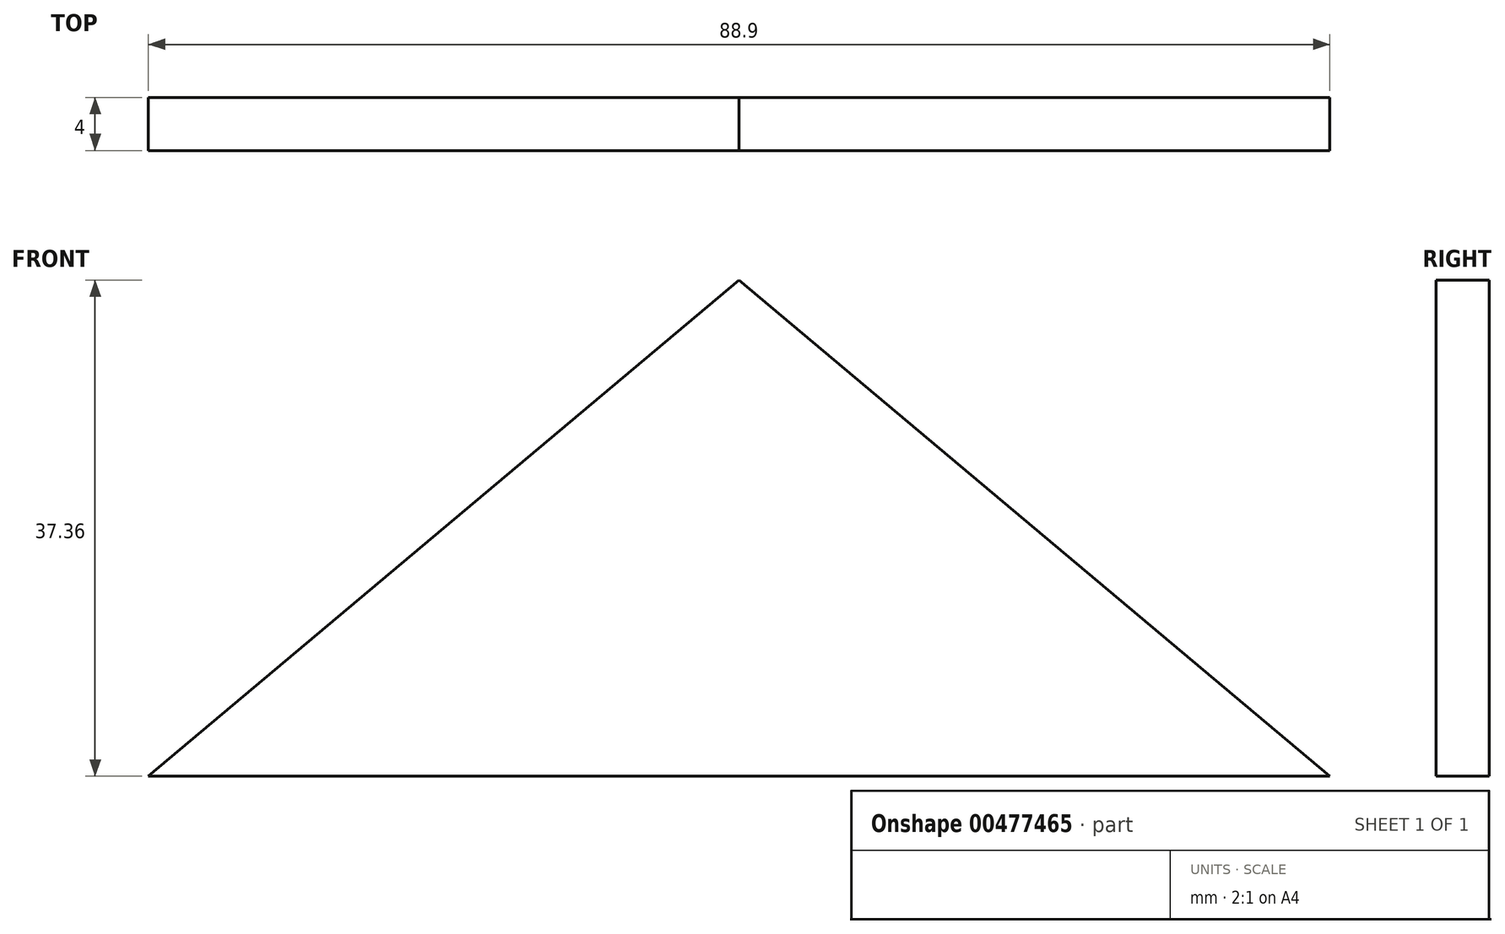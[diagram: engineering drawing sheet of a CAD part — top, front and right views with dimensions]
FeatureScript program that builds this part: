
annotation { "Feature Type Name" : "Feature", "Feature Type Description" : "" }
export const myFeature = defineFeature(function(context is Context, id is Id, definition is map)
    precondition{}
    {
        {
            var Q0;
            Q0=qCreatedBy(makeId("Front.planeOp"),FACE);
            var sketch = newSketch(context, id + "F0", { "sketchPlane" : qUnion([Q0])});
            skLineSegment(sketch, "E0.top", {"start": v(-44.45, -37.36) * mm, "end": v(44.45, -37.36) * mm});
            skPoint(sketch, "E0.middle", {"position": v(0, 0) * mm});
            skLineSegment(sketch, "E1", {"start": v(-44.45, -37.36) * mm, "end": v(0, 0) * mm});
            skLineSegment(sketch, "E2.MirrorCS", {"start": v(44.45, -37.36) * mm, "end": v(0, 0) * mm});
            skSolve(sketch);
        }
        {
            var Q0;
            Q0 = qSketchRegion(id + "F0", true);
            extrude(context, id + "F1", {"entities" : qUnion([Q0]), "depth" : 4 * mm});
        }
    });
